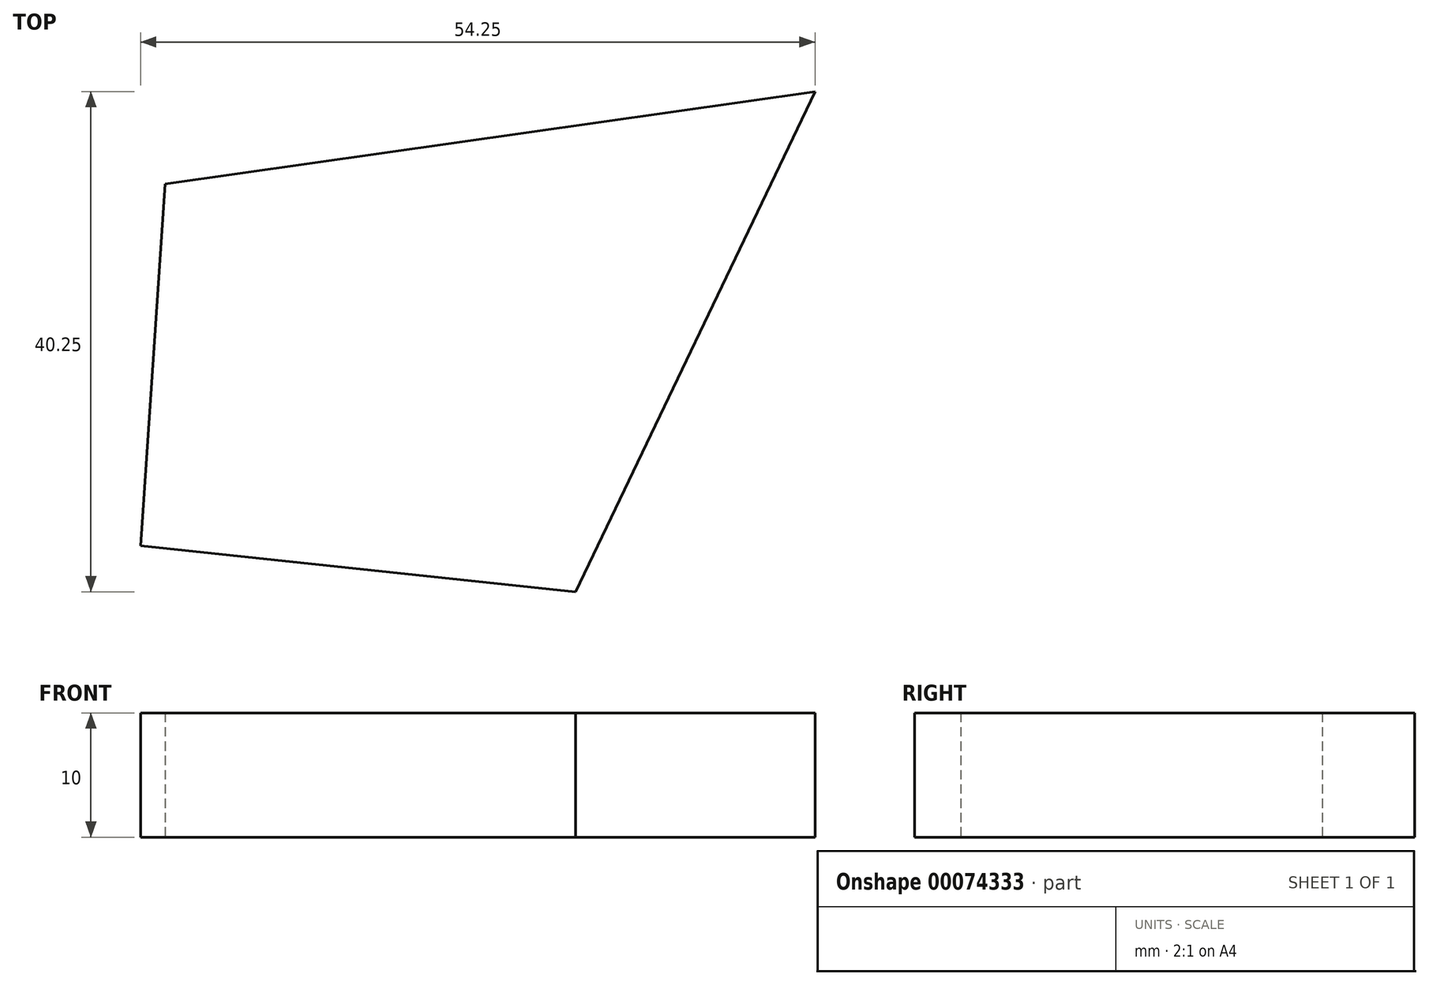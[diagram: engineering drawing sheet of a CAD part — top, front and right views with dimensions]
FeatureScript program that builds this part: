
annotation { "Feature Type Name" : "Feature", "Feature Type Description" : "" }
export const myFeature = defineFeature(function(context is Context, id is Id, definition is map)
    precondition{}
    {
        {
            var Q0;
            Q0=qCreatedBy(makeId("Top.planeOp"),FACE);
            var sketch = newSketch(context, id + "F0", { "sketchPlane" : qUnion([Q0])});
            skLineSegment(sketch, "E0", {"start": v(-20.56, 5.9) * mm, "end": v(-18.6, 35) * mm});
            skLineSegment(sketch, "E1", {"start": v(-18.6, 35) * mm, "end": v(33.69, 42.44) * mm});
            skLineSegment(sketch, "E2", {"start": v(33.69, 42.44) * mm, "end": v(14.44, 2.19) * mm});
            skLineSegment(sketch, "E3", {"start": v(14.44, 2.19) * mm, "end": v(-20.56, 5.9) * mm});
            skSolve(sketch);
        }
        {
            var Q0;
            Q0=makeQuery(id+"F0.imprint","IMPRINT",FACE,{"disambiguationData":[TD([[makeQuery(id+"F0.imprint","IMPRINT",EDGE,{"derivedFrom":sQuery(id+"F0.wireOp",EDGE,"E0")}),-1.0]])]});
            extrude(context, id + "F1", {"entities" : qUnion([Q0]), "depth" : 10 * mm});
        }
    });
